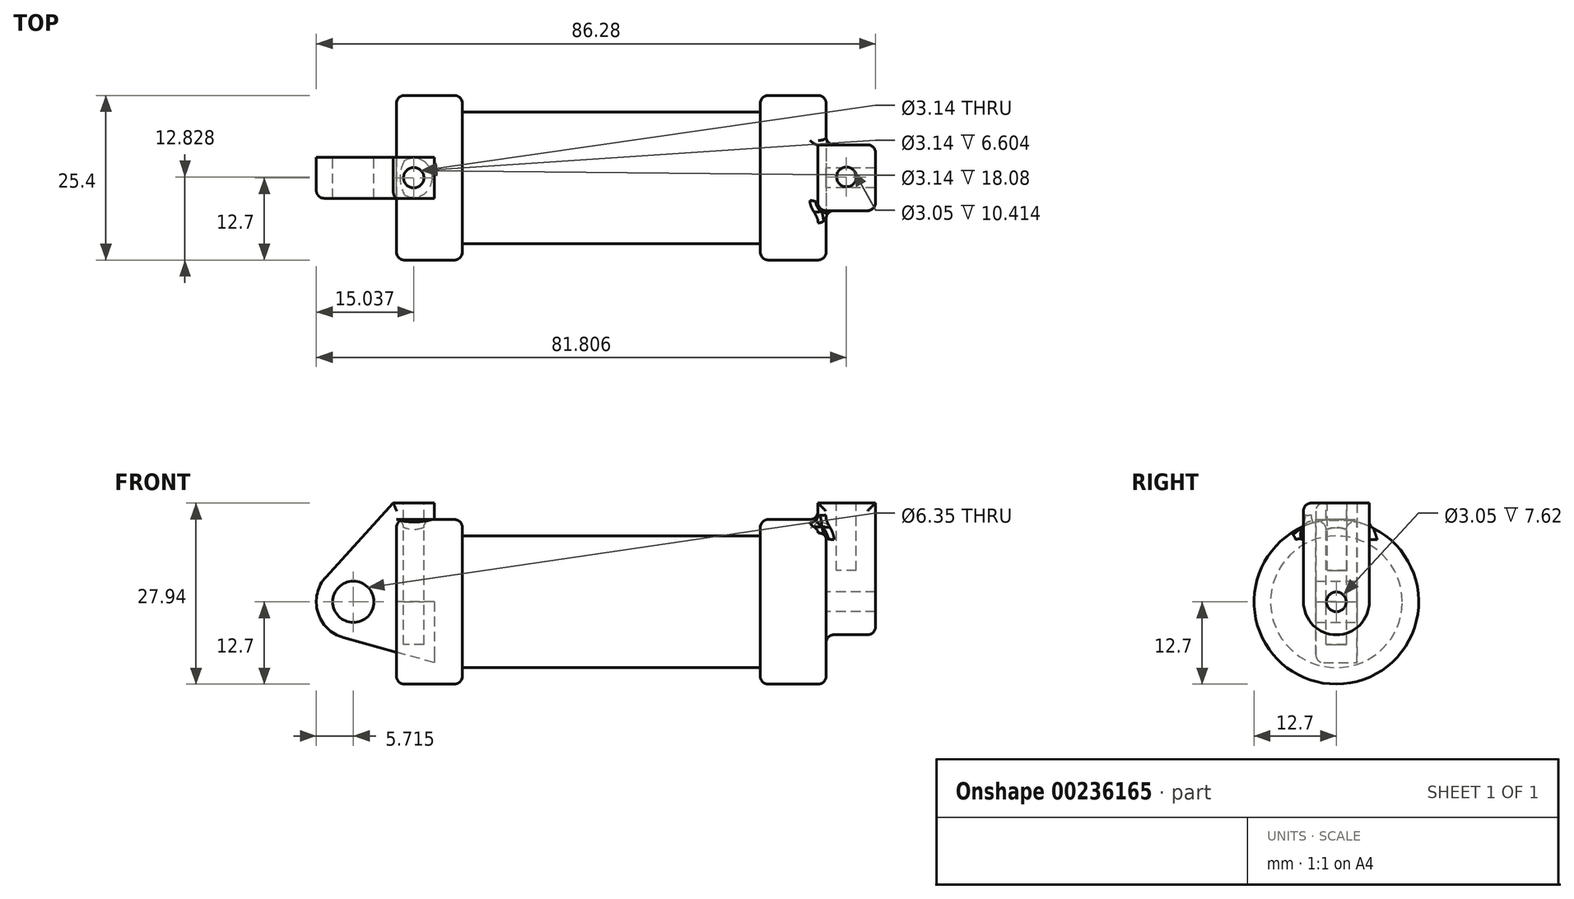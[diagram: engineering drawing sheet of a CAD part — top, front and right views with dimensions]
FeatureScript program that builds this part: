
annotation { "Feature Type Name" : "Feature", "Feature Type Description" : "" }
export const myFeature = defineFeature(function(context is Context, id is Id, definition is map)
    precondition{}
    {
        {
            var Q0;
            Q0=qCreatedBy(makeId("Front.planeOp"),FACE);
            var sketch = newSketch(context, id + "F0", { "sketchPlane" : qUnion([Q0])});
            skLineSegment(sketch, "E0", {"start": v(0, 0) * mm, "end": v(0, 12.7) * mm});
            skLineSegment(sketch, "E1", {"start": v(0, 12.7) * mm, "end": v(10.16, 12.7) * mm});
            skLineSegment(sketch, "E2", {"start": v(10.16, 12.7) * mm, "end": v(10.16, 10.16) * mm});
            skLineSegment(sketch, "E3", {"start": v(10.16, 10.16) * mm, "end": v(56.13, 10.16) * mm});
            skLineSegment(sketch, "E4", {"start": v(56.13, 10.16) * mm, "end": v(56.13, 12.7) * mm});
            skLineSegment(sketch, "E5", {"start": v(56.13, 12.7) * mm, "end": v(66.3, 12.7) * mm});
            skLineSegment(sketch, "E6", {"start": v(66.3, 12.7) * mm, "end": v(66.3, 0) * mm});
            skLineSegment(sketch, "E7", {"start": v(66.3, 0) * mm, "end": v(0, 0) * mm});
            skLineSegment(sketch, "E8", {"start": v(5.84, 15.24) * mm, "end": v(-0.5, 15.24) * mm});
            skLineSegment(sketch, "E9", {"start": v(-0.5, 15.24) * mm, "end": v(-10.88, 3.85) * mm});
            skLineSegment(sketch, "E10", {"start": v(0, 0) * mm, "end": v(-6.65, 0) * mm});
            skCircle(sketch, "E11", {"center": v(-6.65, 0) * mm, "radius": 5.72 * mm});
            skCircle(sketch, "E12", {"center": v(-6.65, 0) * mm, "radius": 3.18 * mm});
            skLineSegment(sketch, "E13", {"start": v(5.84, 15.24) * mm, "end": v(5.84, -9.4) * mm});
            skLineSegment(sketch, "E14", {"start": v(5.84, -9.4) * mm, "end": v(-8.18, -5.5) * mm});
            skSolve(sketch);
        }
        {
            var Q0;
            {var subQ0=sQuery(id+"F0.wireOp",EDGE,"E2");Q0=makeQuery(id+"F0.imprint","IMPRINT",FACE,{"disambiguationData":[TD([[makeQuery(id+"F0.imprint","IMPRINT",EDGE,{"derivedFrom":subQ0}),-1.0]])]});}
            var Q1;
            {var subQ0=sQuery(id+"F0.wireOp",EDGE,"E0");Q1=makeQuery(id+"F0.imprint","IMPRINT",FACE,{"disambiguationData":[TD([[makeQuery(id+"F0.imprint","IMPRINT",EDGE,{"derivedFrom":subQ0}),-1.0]])]});}
            var Q2;
            Q2=sQuery(id+"F0.wireOp",EDGE,"E7");
            revolve(context, id + "F1", {"entities" : qUnion([Q0, Q1]), "axis" : qUnion([Q2]), "revolveType" : RevolveType.FULL});
        }
        {
            var Q0;
            {var subQ3=sQuery(id+"F0.wireOp",EDGE,"E0");Q0=makeQuery(id+"F0.imprint","IMPRINT",FACE,{"disambiguationData":[TD([[makeQuery(id+"F0.imprint","IMPRINT",EDGE,{"derivedFrom":subQ3}),1.0]])]});}
            var Q1;
            {var subQ4=sQuery(id+"F0.wireOp",EDGE,"E12");Q1=makeQuery(id+"F0.imprint","IMPRINT",FACE,{"disambiguationData":[TD([[makeQuery(id+"F0.imprint","IMPRINT",EDGE,{"derivedFrom":subQ4}),-1.0]])]});}
            var Q2;
            {var subQ0=sQuery(id+"F0.wireOp",EDGE,"E14");Q2=makeQuery(id+"F0.imprint","IMPRINT",FACE,{"disambiguationData":[TD([[makeQuery(id+"F0.imprint","IMPRINT",EDGE,{"derivedFrom":subQ0}),-1.0]])]});}
            extrude(context, id + "F2", {"entities" : qUnion([Q0, Q1, Q2]), "endBound" : BoundingType.SYMMETRIC, "depth" : 6.35 * mm});
        }
        {
            var Q0;
            Q0=makeQuery(id+"F1.opRevolve","SWEPT_FACE",FACE,{"disambiguationData":[OSD([sQuery(id+"F0.wireOp",EDGE,"E6")])]});
            var sketch = newSketch(context, id + "F3", { "sketchPlane" : qUnion([Q0])});
            skCircle(sketch, "E15", {"center": v(0, 0) * mm, "radius": 1.52 * mm});
            skCircle(sketch, "E16", {"center": v(0, 0) * mm, "radius": 5.08 * mm});
            skLineSegment(sketch, "E17", {"start": v(-5.08, 0) * mm, "end": v(-5.08, 15.24) * mm});
            skLineSegment(sketch, "E18", {"start": v(5.08, 0) * mm, "end": v(5.08, 15.24) * mm});
            skLineSegment(sketch, "E19", {"start": v(5.08, 15.24) * mm, "end": v(-5.08, 15.24) * mm});
            skSolve(sketch);
        }
        {
            var Q0;
            {var subQ0=sQuery(id+"F3.wireOp",EDGE,"E19");Q0=makeQuery(id+"F3.imprint","IMPRINT",FACE,{"disambiguationData":[TD([[makeQuery(id+"F3.imprint","IMPRINT",EDGE,{"derivedFrom":subQ0}),1.0]])]});}
            var Q1;
            {var subQ0=sQuery(id+"F3.wireOp",EDGE,"E17");var subQ1=sQuery(id+"F3.wireOp",EDGE,"E16");var subQ2=makeQuery(id+"F3.imprint","INTERSECT",VERTEX,{"derivedFrom":[subQ1,subQ0]});Q1=makeQuery(id+"F3.imprint","IMPRINT",FACE,{"disambiguationData":[TD([[makeQuery(id+"F3.imprint","IMPRINT",EDGE,{"disambiguationData":[TD([[subQ2,1.0]])],"derivedFrom":subQ1}),-1.0]])]});}
            var Q2;
            Q2=makeQuery(id+"F3.imprint","IMPRINT",FACE,{"disambiguationData":[TD([[makeQuery(id+"F3.imprint","IMPRINT",EDGE,{"derivedFrom":sQuery(id+"F3.wireOp",EDGE,"E15")}),-1.0]])]});
            extrude(context, id + "F4", {"entities" : qUnion([Q0, Q1, Q2]), "operationType" : NewBodyOperationType.ADD, "depth" : 7.62 * mm});
        }
        {
            var Q0;
            {var subQ0=sQuery(id+"F3.wireOp",EDGE,"E17");var subQ1=sQuery(id+"F3.wireOp",EDGE,"E16");var subQ2=makeQuery(id+"F3.imprint","INTERSECT",VERTEX,{"derivedFrom":[subQ1,subQ0]});Q0=makeQuery(id+"F3.imprint","IMPRINT",FACE,{"disambiguationData":[TD([[makeQuery(id+"F3.imprint","IMPRINT",EDGE,{"disambiguationData":[TD([[subQ2,1.0]])],"derivedFrom":subQ1}),-1.0]])]});}
            var Q1;
            {var subQ0=sQuery(id+"F3.wireOp",EDGE,"E19");Q1=makeQuery(id+"F3.imprint","IMPRINT",FACE,{"disambiguationData":[TD([[makeQuery(id+"F3.imprint","IMPRINT",EDGE,{"derivedFrom":subQ0}),1.0]])]});}
            var Q2;
            Q2=makeQuery(id+"F3.imprint","IMPRINT",FACE,{"disambiguationData":[TD([[makeQuery(id+"F3.imprint","IMPRINT",EDGE,{"derivedFrom":sQuery(id+"F3.wireOp",EDGE,"E15")}),-1.0]])]});
            var Q3;
            Q3=makeQuery(id+"F3.imprint","IMPRINT",FACE,{"disambiguationData":[TD([[makeQuery(id+"F3.imprint","IMPRINT",EDGE,{"derivedFrom":sQuery(id+"F3.wireOp",EDGE,"E15")}),1.0]])]});
            extrude(context, id + "F5", {"entities" : qUnion([Q0, Q1, Q2, Q3]), "operationType" : NewBodyOperationType.ADD, "oppositeDirection" : true, "depth" : 1.27 * mm});
        }
        {
            var Q0;
            Q0=makeQuery(id+"F2.opExtrude","SWEPT_FACE",FACE,{"disambiguationData":[OSD([sQuery(id+"F0.wireOp",EDGE,"E8")])]});
            var sketch = newSketch(context, id + "F6", { "sketchPlane" : qUnion([Q0])});
            skLineSegment(sketch, "E20", {"start": v(-0.5, 0) * mm, "end": v(5.84, 0) * mm});
            skCircle(sketch, "E21", {"center": v(2.67, 0) * mm, "radius": 1.57 * mm});
            skSolve(sketch);
        }
        {
            var Q0;
            Q0=sQuery(id+"F6.wireOp",EDGE,"E21");
            extrude(context, id + "F7", {"bodyType" : ToolBodyType.SURFACE, "surfaceEntities" : qUnion([Q0]), "oppositeDirection" : true, "depth" : 22.35 * mm});
        }
        {
            var Q0;
            Q0 = qSketchRegion(id + "F6", true);
            extrude(context, id + "F8", {"entities" : qUnion([Q0]), "operationType" : NewBodyOperationType.REMOVE, "oppositeDirection" : true, "depth" : 21.84 * mm});
        }
        {
            var Q0;
            {var subQ0=sQuery(id+"F3.wireOp",EDGE,"E19");Q0=makeQuery(id+"F5.boolean.opBoolean","MERGE",FACE,{"derivedFrom":[makeQuery(id+"F4.opExtrude","SWEPT_FACE",FACE,{"disambiguationData":[OSD([subQ0])]}),makeQuery(id+"F5.opExtrude","SWEPT_FACE",FACE,{"disambiguationData":[OSD([subQ0])]})]});}
            var sketch = newSketch(context, id + "F9", { "sketchPlane" : qUnion([Q0])});
            skCircle(sketch, "E22", {"center": v(69.44, 0.13) * mm, "radius": 1.52 * mm});
            skSolve(sketch);
        }
        {
            var Q0;
            Q0 = qSketchRegion(id + "F9", true);
            extrude(context, id + "F10", {"entities" : qUnion([Q0]), "operationType" : NewBodyOperationType.REMOVE, "oppositeDirection" : true, "depth" : 10.4 * mm});
        }
        {
            var Q0;
            Q0=makeQuery(id+"F1.opRevolve","SWEPT_FACE",FACE,{"disambiguationData":[OSD([sQuery(id+"F0.wireOp",EDGE,"E0")])]});
            var Q1;
            Q1=makeQuery(id+"F1.opRevolve","SWEPT_FACE",FACE,{"disambiguationData":[OSD([sQuery(id+"F0.wireOp",EDGE,"E1")])]});
            var Q2;
            Q2=makeQuery(id+"F1.opRevolve","SWEPT_FACE",FACE,{"disambiguationData":[OSD([sQuery(id+"F0.wireOp",EDGE,"E5")])]});
            var Q3;
            {var subQ0=sQuery(id+"F3.wireOp",EDGE,"E17");Q3=makeQuery(id+"F5.boolean.opBoolean","MERGE",FACE,{"derivedFrom":[makeQuery(id+"F4.opExtrude","SWEPT_FACE",FACE,{"disambiguationData":[OSD([subQ0])]}),makeQuery(id+"F5.opExtrude","SWEPT_FACE",FACE,{"disambiguationData":[OSD([subQ0])]})]});}
            var Q4;
            Q4=makeQuery(id+"F2.opExtrude","CAP_EDGE",EDGE,{"disambiguationData":[OSD([sQuery(id+"F0.wireOp",EDGE,"E9")])],"isStart":false});
            var Q5;
            Q5=makeQuery(id+"F2.opExtrude","CAP_EDGE",EDGE,{"disambiguationData":[OSD([sQuery(id+"F0.wireOp",EDGE,"E11")])],"isStart":false});
            var Q6;
            Q6=makeQuery(id+"F2.opExtrude","CAP_EDGE",EDGE,{"disambiguationData":[OSD([sQuery(id+"F0.wireOp",EDGE,"E14")])],"isStart":false});
            var Q7;
            Q7=makeQuery(id+"F2.opExtrude","CAP_EDGE",EDGE,{"disambiguationData":[OSD([sQuery(id+"F0.wireOp",EDGE,"E8")])],"isStart":false});
            fillet(context, id + "F11", {"entities" : qUnion([Q0, Q1, Q2, Q3, Q4, Q5, Q6, Q7]), "radius" : 1.23 * mm, "tangentPropagation" : true, "allowEdgeOverflow" : false});
        }
    });
